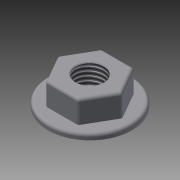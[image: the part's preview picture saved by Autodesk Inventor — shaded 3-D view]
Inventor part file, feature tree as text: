
AUTODESK INVENTOR PART (.ipt)
format: ipt  version: 2015 (Build 190159000, 159)  size: 143,360 bytes
history: native  units: mm
features: extrude x3, sketch x3, chamfer x2, thread x1, fillet x1
ambient origin geometry x8: Origin, YZ Plane, XZ Plane, XY Plane, X Axis, Y Axis, Z Axis, Center Point
bodies: 实体1 (feature_tree)
feature tree (10):
  extrude  "拉伸1"  Depth=2.0mm TaperAngle=0.0deg
  extrude  "拉伸2"  Depth=20.0mm
  extrude  "拉伸3"  Depth=10.0mm
  thread  "螺纹1"  [1 undecoded]
  fillet  "圆角1"  Radius=10.0mm
  chamfer  "倒角1"  Distance=1.0mm
  chamfer  "倒角2"  Distance=2.0mm Angle=45.0deg
  sketch  "草图1"  dims[d0=30.0mm d1=2.0mm d2=0.0mm]
  sketch  "草图2"  dims[d3=1.986024mm d4=20.0mm]
  sketch  "草图3"  dims[d5=8.0mm d6=0.0mm d7=10.0mm d8=8.0mm d9=0.0mm d10=10.0mm d11=0.0mm d12=1.0mm d13=0.25mm d14=2.0mm d15=45.0deg d16=0.25mm d17=2.0mm d18=45.0deg]
note: 1 required parameter value undecoded (feature->parameter linkage not recoverable at this tier; creation-order binding heuristic only, values carry confidence <= 0.55)
